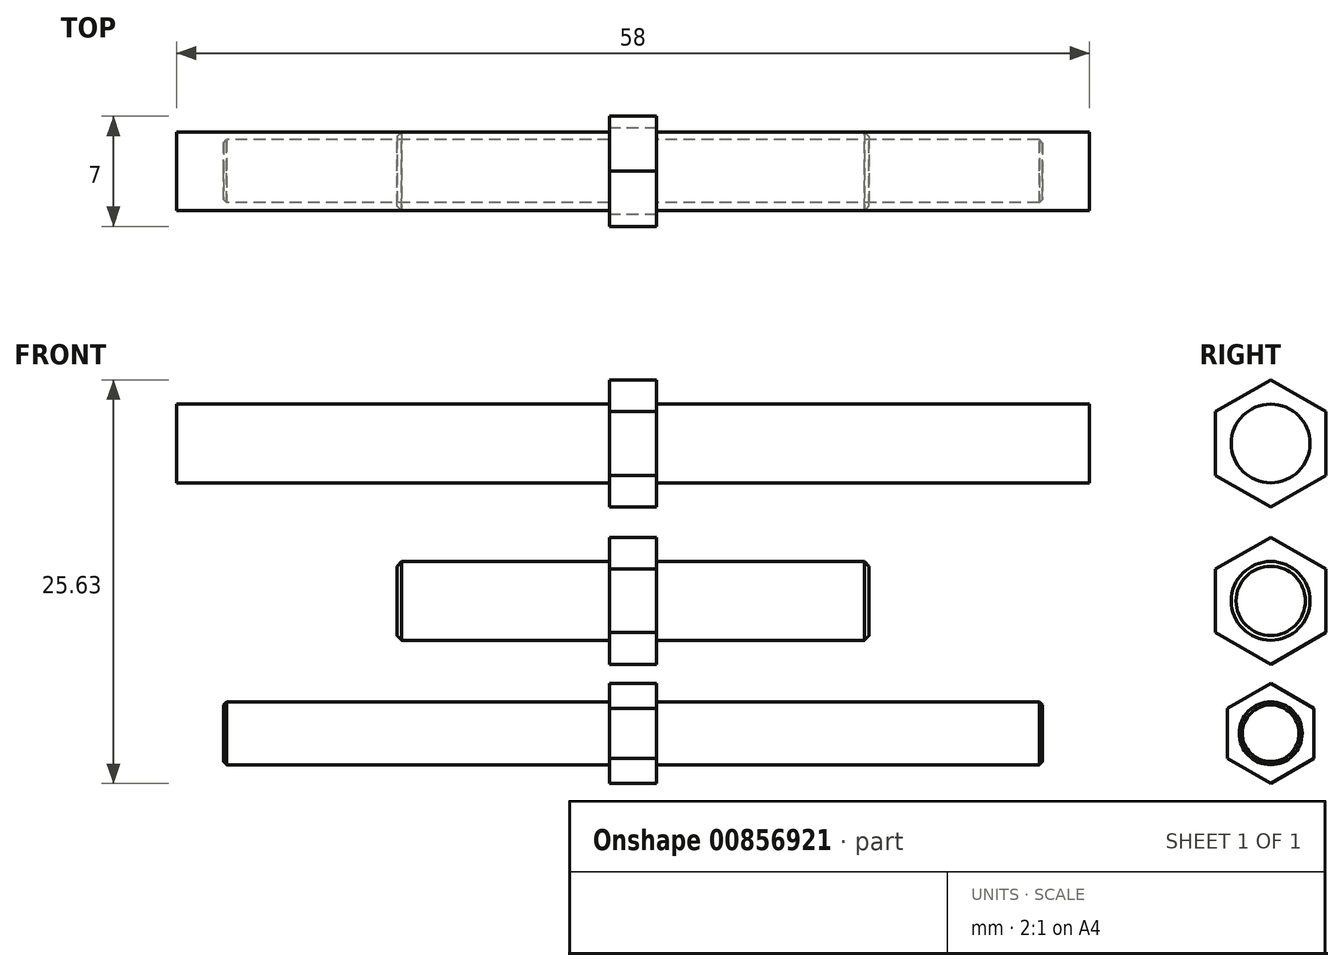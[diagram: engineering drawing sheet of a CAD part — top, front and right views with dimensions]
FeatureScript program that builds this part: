
annotation { "Feature Type Name" : "Feature", "Feature Type Description" : "" }
export const myFeature = defineFeature(function(context is Context, id is Id, definition is map)
    precondition{}
    {
        {
            var Q0;
            Q0=qCreatedBy(makeId("Right.planeOp"),FACE);
            var sketch = newSketch(context, id + "F0", { "sketchPlane" : qUnion([Q0])});
            skCircle(sketch, "E0", {"center": v(0, 0) * mm, "radius": 2 * mm});
            skSolve(sketch);
        }
        {
            var Q0;
            Q0 = qSketchRegion(id + "F0", true);
            extrude(context, id + "F1", {"entities" : qUnion([Q0]), "depth" : 52 * mm, "offsetDistance" : 25 * mm, "symmetric" : true});
        }
        {
            var Q0;
            Q0=qCreatedBy(makeId("Right.planeOp"),FACE);
            var sketch = newSketch(context, id + "F2", { "sketchPlane" : qUnion([Q0])});
            skCircle(sketch, "E1.cCircle", {"center": v(0, 0) * mm, "radius": 2.75 * mm, "construction": true});
            skLineSegment(sketch, "E1.0", {"start": v(2.75, 1.59) * mm, "end": v(2.75, -1.59) * mm});
            skLineSegment(sketch, "E1.1", {"start": v(2.75, -1.59) * mm, "end": v(0, -3.18) * mm});
            skLineSegment(sketch, "E1.2", {"start": v(0, -3.18) * mm, "end": v(-2.75, -1.59) * mm});
            skLineSegment(sketch, "E1.3", {"start": v(-2.75, -1.59) * mm, "end": v(-2.75, 1.59) * mm});
            skLineSegment(sketch, "E1.4", {"start": v(-2.75, 1.59) * mm, "end": v(0, 3.18) * mm});
            skLineSegment(sketch, "E1.5", {"start": v(0, 3.18) * mm, "end": v(2.75, 1.59) * mm});
            skPoint(sketch, "E1.0.midPoint", {"position": v(2.75, 0) * mm});
            skLineSegment(sketch, "E2", {"start": v(0, 0) * mm, "end": v(0, -4.6) * mm, "construction": true});
            skSolve(sketch);
        }
        {
            var Q0;
            Q0=makeQuery(id+"F2.imprint","IMPRINT",FACE,{"disambiguationData":[TD([[makeQuery(id+"F2.imprint","IMPRINT",EDGE,{"derivedFrom":sQuery(id+"F2.wireOp",EDGE,"E1.0")}),-1.0]])]});
            extrude(context, id + "F3", {"entities" : qUnion([Q0]), "operationType" : NewBodyOperationType.ADD, "depth" : 3 * mm, "offsetDistance" : 25 * mm, "symmetric" : true});
        }
        {
            var Q0;
            Q0=qCreatedBy(makeId("Right.planeOp"),FACE);
            var sketch = newSketch(context, id + "F4", { "sketchPlane" : qUnion([Q0])});
            skCircle(sketch, "E3", {"center": v(0, 8.41) * mm, "radius": 2.5 * mm});
            skSolve(sketch);
        }
        {
            var Q0;
            Q0=makeQuery(id+"F4.imprint","IMPRINT",FACE,{"disambiguationData":[TD([[makeQuery(id+"F4.imprint","IMPRINT",EDGE,{"derivedFrom":sQuery(id+"F4.wireOp",EDGE,"E3")}),1.0]])]});
            extrude(context, id + "F5", {"entities" : qUnion([Q0]), "depth" : 30 * mm, "offsetDistance" : 25 * mm, "symmetric" : true});
        }
        {
            var Q0;
            Q0=qCreatedBy(makeId("Right.planeOp"),FACE);
            var sketch = newSketch(context, id + "F6", { "sketchPlane" : qUnion([Q0])});
            skCircle(sketch, "E4.0", {"center": v(0, 8.41) * mm, "radius": 2.5 * mm, "construction": true});
            skLineSegment(sketch, "E5", {"start": v(0, 8.41) * mm, "end": v(0, 14.45) * mm, "construction": true});
            skCircle(sketch, "E6.cCircle", {"center": v(0, 8.41) * mm, "radius": 3.5 * mm, "construction": true});
            skLineSegment(sketch, "E6.0", {"start": v(0, 12.45) * mm, "end": v(3.5, 10.43) * mm});
            skLineSegment(sketch, "E6.1", {"start": v(3.5, 10.43) * mm, "end": v(3.5, 6.4) * mm});
            skLineSegment(sketch, "E6.2", {"start": v(3.5, 6.4) * mm, "end": v(0, 4.37) * mm});
            skLineSegment(sketch, "E6.3", {"start": v(0, 4.37) * mm, "end": v(-3.5, 6.4) * mm});
            skLineSegment(sketch, "E6.4", {"start": v(-3.5, 6.4) * mm, "end": v(-3.5, 10.43) * mm});
            skLineSegment(sketch, "E6.5", {"start": v(-3.5, 10.43) * mm, "end": v(0, 12.45) * mm});
            skPoint(sketch, "E6.0.midPoint", {"position": v(1.75, 11.44) * mm});
            skSolve(sketch);
        }
        {
            var Q0;
            Q0=makeQuery(id+"F6.imprint","IMPRINT",FACE,{"disambiguationData":[TD([[makeQuery(id+"F6.imprint","IMPRINT",EDGE,{"derivedFrom":sQuery(id+"F6.wireOp",EDGE,"E6.0")}),-1.0]])]});
            extrude(context, id + "F7", {"entities" : qUnion([Q0]), "operationType" : NewBodyOperationType.ADD, "depth" : 3 * mm, "offsetDistance" : 25 * mm, "symmetric" : true});
        }
        {
            var Q0;
            Q0=makeQuery(id+"F1.opExtrude","CAP_EDGE",EDGE,{"disambiguationData":[OSD([sQuery(id+"F0.wireOp",EDGE,"E0")])],"isStart":false});
            var Q1;
            Q1=makeQuery(id+"F1.opExtrude","CAP_EDGE",EDGE,{"disambiguationData":[OSD([sQuery(id+"F0.wireOp",EDGE,"E0")])],"isStart":true});
            chamfer(context, id + "F8", {"entities" : qUnion([Q0, Q1]), "width" : 0.2 * mm, "tangentPropagation" : true});
        }
        {
            var Q0;
            Q0=makeQuery(id+"F5.opExtrude","SWEPT_BODY",BODY,{"disambiguationData":[OSD([sQuery(id+"F4.wireOp",EDGE,"E3")])]});
            transform(context, id + "F9", {"entities" : qUnion([Q0]), "transformType" : TransformType.TRANSLATION_3D, "dx" : 0 * mm, "dy" : 0 * mm, "dz" : 10 * mm, "makeCopy" : true});
        }
        {
            var Q0;
            Q0=makeQuery(id+"F5.opExtrude","CAP_EDGE",EDGE,{"disambiguationData":[OSD([sQuery(id+"F4.wireOp",EDGE,"E3")])],"isStart":true});
            var Q1;
            Q1=makeQuery(id+"F5.opExtrude","CAP_EDGE",EDGE,{"disambiguationData":[OSD([sQuery(id+"F4.wireOp",EDGE,"E3")])],"isStart":false});
            chamfer(context, id + "F10", {"entities" : qUnion([Q0, Q1]), "width" : 0.3 * mm, "tangentPropagation" : true});
        }
        {
            var Q0;
            Q0=makeQuery(id+"F9.opPattern","COPY",FACE,{"derivedFrom":makeQuery(id+"F5.opExtrude","CAP_FACE",FACE,{"disambiguationData":[OSD([sQuery(id+"F4.wireOp",EDGE,"E3")])],"isStart":true}),"instanceName":"1"});
            extrude(context, id + "F11", {"entities" : qUnion([Q0]), "operationType" : NewBodyOperationType.ADD, "depth" : ((58 - 30) / 2) * mm, "offsetDistance" : 25 * mm});
        }
        {
            var Q0;
            Q0=makeQuery(id+"F9.opPattern","COPY",FACE,{"derivedFrom":makeQuery(id+"F5.opExtrude","CAP_FACE",FACE,{"disambiguationData":[OSD([sQuery(id+"F4.wireOp",EDGE,"E3")])],"isStart":false}),"instanceName":"1"});
            extrude(context, id + "F12", {"entities" : qUnion([Q0]), "operationType" : NewBodyOperationType.ADD, "depth" : 14 * mm, "offsetDistance" : 25 * mm});
        }
    });
